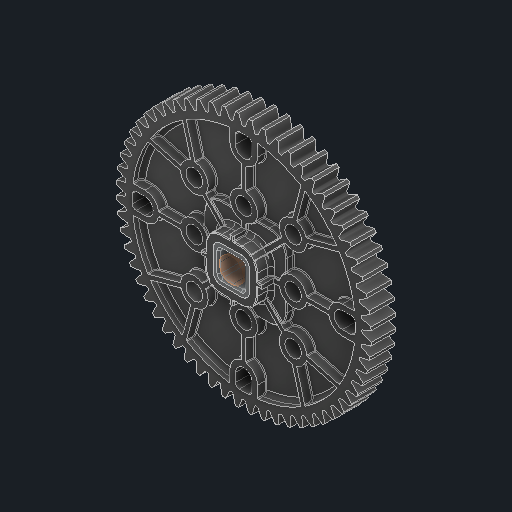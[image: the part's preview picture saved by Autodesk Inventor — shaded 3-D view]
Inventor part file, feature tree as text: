
AUTODESK INVENTOR PART (.ipt)
format: ipt  version: 2025 (Build 290162000, 162)  size: 3,763,200 bytes
history: native  units: in
note: dims shown in document units (in); Inventor stores cm internally (conversion verified against a paired STEP export)
features: other x3, extrude x3, sketch x2
ambient origin geometry x8: Origin, YZ Plane, XZ Plane, XY Plane, X Axis, Y Axis, Z Axis, Center Point
bodies: Solid1 (feature_tree), Solid2 (feature_tree)
feature tree (8):
  other  "276-7748-001_OVERMOLD Rev3_60T 24DP Gear Rev1_1:1"
  extrude  "Extrusion1"  Depth=0.3937in TaperAngle=0.0deg
  extrude  "Extrusion2"  Depth=0.125in TaperAngle=0.0deg
  other  "Srf1"
  sketch  "Sketch2"  dims[d0=0.25in d1=0.3937in d2=0.0in]
  sketch  "Sketch3"  dims[d3=0.125in d4=0.0in d5=0.125in d6=0.0in]
  other  "276-7573-002 Rev7_2:1"
  extrude  "ExtrusionSrf1"  [1 undecoded]
note: 1 required parameter value undecoded (feature->parameter linkage not recoverable at this tier; creation-order binding heuristic only, values carry confidence <= 0.55)
